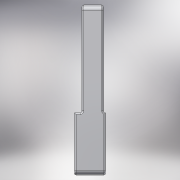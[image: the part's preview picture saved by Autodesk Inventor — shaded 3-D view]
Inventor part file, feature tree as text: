
AUTODESK INVENTOR PART (.ipt)
format: ipt  version: 2018 (Build 220112000, 112)  size: 315,904 bytes
history: native  units: mm
features: extrude x7, fillet x7, other x3, draft x1, chamfer x1
ambient origin geometry x8: Origin, YZ Plane, XZ Plane, XY Plane, X Axis, Y Axis, Z Axis, Center Point
bodies: Solid1 (feature_tree)
feature tree (19):
  other  "Key Sketch"
  extrude  "Upper Key"  Depth=10.0mm
  extrude  "Lower Key"  Depth=1.0mm
  other  "Hinge Cut Sketch"
  extrude  "Hinge Cut"  Depth=10.0mm TaperAngle=0.0deg
  extrude  "Hinge Cut 2"  Depth=3.0mm
  other  "Lever Sketch"
  extrude  "Vertical Lever"  Depth=3.0mm
  extrude  "Horizontal Lever"  Depth=33.6625mm
  extrude  "Spring Hook"  Depth=0.5mm
  draft  "FaceDraft3"
  chamfer  "Chamfer1"  Distance=3.0mm
  fillet  "Fillet9"  Radius=6.0mm
  fillet  "Fillet10"  Radius=4.0mm
  fillet  "Fillet5"  Radius=10.0mm
  fillet  "Fillet4"  [1 undecoded]
  fillet  "Fillet11"  Radius=3.0mm
  fillet  "Fillet15"  Radius=2.3mm
  fillet  "Fillet14"  Radius=5.3mm
note: 1 required parameter value undecoded (feature->parameter linkage not recoverable at this tier; creation-order binding heuristic only, values carry confidence <= 0.55)
